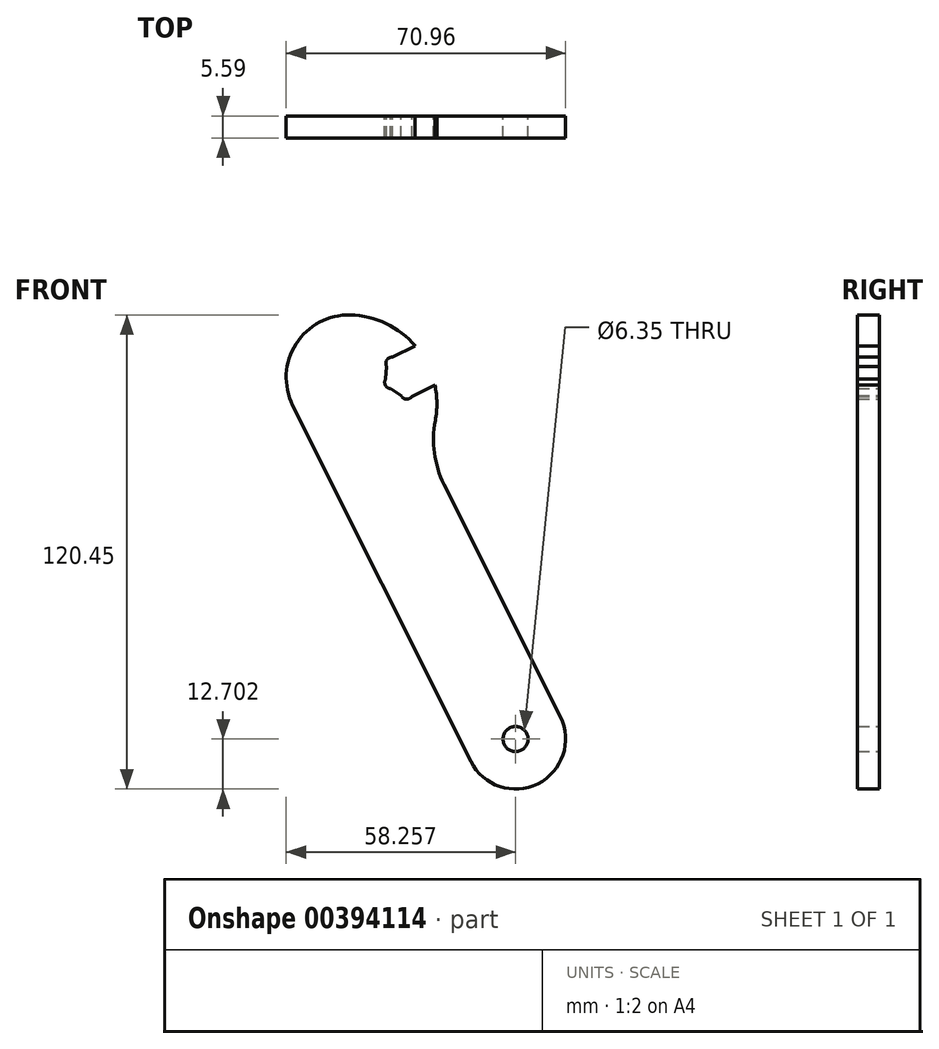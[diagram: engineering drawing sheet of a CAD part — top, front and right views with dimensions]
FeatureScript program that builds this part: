
annotation { "Feature Type Name" : "Feature", "Feature Type Description" : "" }
export const myFeature = defineFeature(function(context is Context, id is Id, definition is map)
    precondition{}
    {
        {
            var Q0;
            Q0=qCreatedBy(makeId("Front.planeOp"),FACE);
            var sketch = newSketch(context, id + "F0", { "sketchPlane" : qUnion([Q0])});
            skCircle(sketch, "E0", {"center": v(-169.2, -191.67) * mm, "radius": 3.18 * mm, "construction": true});
            skCircle(sketch, "E1.0.1.0", {"center": v(-169.2, -166.27) * mm, "radius": 3.18 * mm, "construction": true});
            skCircle(sketch, "E1.0.2.0", {"center": v(-169.2, -140.87) * mm, "radius": 3.18 * mm, "construction": true});
            skCircle(sketch, "E1.0.3.0", {"center": v(-169.2, -115.47) * mm, "radius": 3.18 * mm, "construction": true});
            skCircle(sketch, "E1.0.4.0", {"center": v(-169.2, -90.07) * mm, "radius": 3.18 * mm, "construction": true});
            skCircle(sketch, "E1.0.5.0", {"center": v(-169.2, -64.67) * mm, "radius": 3.18 * mm, "construction": true});
            skCircle(sketch, "E1.0.6.0", {"center": v(-169.2, -39.27) * mm, "radius": 3.18 * mm, "construction": true});
            skCircle(sketch, "E1.0.7.0", {"center": v(-169.2, -13.87) * mm, "radius": 3.18 * mm, "construction": true});
            skCircle(sketch, "E1.0.8.0", {"center": v(-169.2, 11.53) * mm, "radius": 3.18 * mm, "construction": true});
            skCircle(sketch, "E1.0.9.0", {"center": v(-169.2, 36.93) * mm, "radius": 3.18 * mm, "construction": true});
            skCircle(sketch, "E1.0.10.0", {"center": v(-169.2, 62.33) * mm, "radius": 3.18 * mm, "construction": true});
            skCircle(sketch, "E1.0.11.0", {"center": v(-169.2, 87.73) * mm, "radius": 3.18 * mm, "construction": true});
            skCircle(sketch, "E1.0.12.0", {"center": v(-169.2, 113.13) * mm, "radius": 3.18 * mm, "construction": true});
            skCircle(sketch, "E1.0.13.0", {"center": v(-169.2, 138.53) * mm, "radius": 3.18 * mm, "construction": true});
            skCircle(sketch, "E1.0.14.0", {"center": v(-169.2, 163.93) * mm, "radius": 3.18 * mm, "construction": true});
            skCircle(sketch, "E1.1.0.0", {"center": v(-143.8, -191.67) * mm, "radius": 3.18 * mm, "construction": true});
            skCircle(sketch, "E1.1.1.0", {"center": v(-143.8, -166.27) * mm, "radius": 3.18 * mm, "construction": true});
            skCircle(sketch, "E1.1.2.0", {"center": v(-143.8, -140.87) * mm, "radius": 3.18 * mm, "construction": true});
            skCircle(sketch, "E1.1.3.0", {"center": v(-143.8, -115.47) * mm, "radius": 3.18 * mm, "construction": true});
            skCircle(sketch, "E1.1.4.0", {"center": v(-143.8, -90.07) * mm, "radius": 3.18 * mm, "construction": true});
            skCircle(sketch, "E1.1.5.0", {"center": v(-143.8, -64.67) * mm, "radius": 3.18 * mm, "construction": true});
            skCircle(sketch, "E1.1.6.0", {"center": v(-143.8, -39.27) * mm, "radius": 3.18 * mm, "construction": true});
            skCircle(sketch, "E1.1.7.0", {"center": v(-143.8, -13.87) * mm, "radius": 3.18 * mm, "construction": true});
            skCircle(sketch, "E1.1.8.0", {"center": v(-143.8, 11.53) * mm, "radius": 3.18 * mm, "construction": true});
            skCircle(sketch, "E1.1.9.0", {"center": v(-143.8, 36.93) * mm, "radius": 3.18 * mm, "construction": true});
            skCircle(sketch, "E1.1.10.0", {"center": v(-143.8, 62.33) * mm, "radius": 3.18 * mm, "construction": true});
            skCircle(sketch, "E1.1.11.0", {"center": v(-143.8, 87.73) * mm, "radius": 3.18 * mm, "construction": true});
            skCircle(sketch, "E1.1.12.0", {"center": v(-143.8, 113.13) * mm, "radius": 3.18 * mm, "construction": true});
            skCircle(sketch, "E1.1.13.0", {"center": v(-143.8, 138.53) * mm, "radius": 3.18 * mm, "construction": true});
            skCircle(sketch, "E1.1.14.0", {"center": v(-143.8, 163.93) * mm, "radius": 3.18 * mm, "construction": true});
            skCircle(sketch, "E1.2.0.0", {"center": v(-118.4, -191.67) * mm, "radius": 3.18 * mm, "construction": true});
            skCircle(sketch, "E1.2.1.0", {"center": v(-118.4, -166.27) * mm, "radius": 3.18 * mm, "construction": true});
            skCircle(sketch, "E1.2.2.0", {"center": v(-118.4, -140.87) * mm, "radius": 3.18 * mm, "construction": true});
            skCircle(sketch, "E1.2.3.0", {"center": v(-118.4, -115.47) * mm, "radius": 3.18 * mm, "construction": true});
            skCircle(sketch, "E1.2.4.0", {"center": v(-118.4, -90.07) * mm, "radius": 3.18 * mm, "construction": true});
            skCircle(sketch, "E1.2.5.0", {"center": v(-118.4, -64.67) * mm, "radius": 3.18 * mm, "construction": true});
            skCircle(sketch, "E1.2.6.0", {"center": v(-118.4, -39.27) * mm, "radius": 3.18 * mm, "construction": true});
            skCircle(sketch, "E1.2.7.0", {"center": v(-118.4, -13.87) * mm, "radius": 3.18 * mm, "construction": true});
            skCircle(sketch, "E1.2.8.0", {"center": v(-118.4, 11.53) * mm, "radius": 3.18 * mm, "construction": true});
            skCircle(sketch, "E1.2.9.0", {"center": v(-118.4, 36.93) * mm, "radius": 3.18 * mm, "construction": true});
            skCircle(sketch, "E1.2.10.0", {"center": v(-118.4, 62.33) * mm, "radius": 3.18 * mm, "construction": true});
            skCircle(sketch, "E1.2.11.0", {"center": v(-118.4, 87.73) * mm, "radius": 3.18 * mm, "construction": true});
            skCircle(sketch, "E1.2.12.0", {"center": v(-118.4, 113.13) * mm, "radius": 3.18 * mm, "construction": true});
            skCircle(sketch, "E1.2.13.0", {"center": v(-118.4, 138.53) * mm, "radius": 3.18 * mm, "construction": true});
            skCircle(sketch, "E1.2.14.0", {"center": v(-118.4, 163.93) * mm, "radius": 3.18 * mm, "construction": true});
            skCircle(sketch, "E1.3.0.0", {"center": v(-93, -191.67) * mm, "radius": 3.18 * mm, "construction": true});
            skCircle(sketch, "E1.3.1.0", {"center": v(-93, -166.27) * mm, "radius": 3.18 * mm, "construction": true});
            skCircle(sketch, "E1.3.2.0", {"center": v(-93, -140.87) * mm, "radius": 3.18 * mm, "construction": true});
            skCircle(sketch, "E1.3.3.0", {"center": v(-93, -115.47) * mm, "radius": 3.18 * mm, "construction": true});
            skCircle(sketch, "E1.3.4.0", {"center": v(-93, -90.07) * mm, "radius": 3.18 * mm, "construction": true});
            skCircle(sketch, "E1.3.5.0", {"center": v(-93, -64.67) * mm, "radius": 3.18 * mm, "construction": true});
            skCircle(sketch, "E1.3.6.0", {"center": v(-93, -39.27) * mm, "radius": 3.18 * mm, "construction": true});
            skCircle(sketch, "E1.3.7.0", {"center": v(-93, -13.87) * mm, "radius": 3.18 * mm, "construction": true});
            skCircle(sketch, "E1.3.8.0", {"center": v(-93, 11.53) * mm, "radius": 3.18 * mm, "construction": true});
            skCircle(sketch, "E1.3.9.0", {"center": v(-93, 36.93) * mm, "radius": 3.18 * mm, "construction": true});
            skCircle(sketch, "E1.3.10.0", {"center": v(-93, 62.33) * mm, "radius": 3.18 * mm, "construction": true});
            skCircle(sketch, "E1.3.11.0", {"center": v(-93, 87.73) * mm, "radius": 3.18 * mm, "construction": true});
            skCircle(sketch, "E1.3.12.0", {"center": v(-93, 113.13) * mm, "radius": 3.18 * mm, "construction": true});
            skCircle(sketch, "E1.3.13.0", {"center": v(-93, 138.53) * mm, "radius": 3.18 * mm, "construction": true});
            skCircle(sketch, "E1.3.14.0", {"center": v(-93, 163.93) * mm, "radius": 3.18 * mm, "construction": true});
            skCircle(sketch, "E1.4.0.0", {"center": v(-67.6, -191.67) * mm, "radius": 3.18 * mm, "construction": true});
            skCircle(sketch, "E1.4.1.0", {"center": v(-67.6, -166.27) * mm, "radius": 3.18 * mm, "construction": true});
            skCircle(sketch, "E1.4.2.0", {"center": v(-67.6, -140.87) * mm, "radius": 3.18 * mm, "construction": true});
            skCircle(sketch, "E1.4.3.0", {"center": v(-67.6, -115.47) * mm, "radius": 3.18 * mm, "construction": true});
            skCircle(sketch, "E1.4.4.0", {"center": v(-67.6, -90.07) * mm, "radius": 3.18 * mm, "construction": true});
            skCircle(sketch, "E1.4.5.0", {"center": v(-67.6, -64.67) * mm, "radius": 3.18 * mm, "construction": true});
            skCircle(sketch, "E1.4.6.0", {"center": v(-67.6, -39.27) * mm, "radius": 3.18 * mm, "construction": true});
            skCircle(sketch, "E1.4.7.0", {"center": v(-67.6, -13.87) * mm, "radius": 3.18 * mm, "construction": true});
            skCircle(sketch, "E1.4.8.0", {"center": v(-67.6, 11.53) * mm, "radius": 3.18 * mm, "construction": true});
            skCircle(sketch, "E1.4.9.0", {"center": v(-67.6, 36.93) * mm, "radius": 3.18 * mm, "construction": true});
            skCircle(sketch, "E1.4.10.0", {"center": v(-67.6, 62.33) * mm, "radius": 3.18 * mm, "construction": true});
            skCircle(sketch, "E1.4.11.0", {"center": v(-67.6, 87.73) * mm, "radius": 3.18 * mm, "construction": true});
            skCircle(sketch, "E1.4.12.0", {"center": v(-67.6, 113.13) * mm, "radius": 3.18 * mm, "construction": true});
            skCircle(sketch, "E1.4.13.0", {"center": v(-67.6, 138.53) * mm, "radius": 3.18 * mm, "construction": true});
            skCircle(sketch, "E1.4.14.0", {"center": v(-67.6, 163.93) * mm, "radius": 3.18 * mm, "construction": true});
            skCircle(sketch, "E1.5.0.0", {"center": v(-42.2, -191.67) * mm, "radius": 3.18 * mm, "construction": true});
            skCircle(sketch, "E1.5.1.0", {"center": v(-42.2, -166.27) * mm, "radius": 3.18 * mm, "construction": true});
            skCircle(sketch, "E1.5.2.0", {"center": v(-42.2, -140.87) * mm, "radius": 3.18 * mm, "construction": true});
            skCircle(sketch, "E1.5.3.0", {"center": v(-42.2, -115.47) * mm, "radius": 3.18 * mm, "construction": true});
            skCircle(sketch, "E1.5.4.0", {"center": v(-42.2, -90.07) * mm, "radius": 3.18 * mm, "construction": true});
            skCircle(sketch, "E1.5.5.0", {"center": v(-42.2, -64.67) * mm, "radius": 3.18 * mm, "construction": true});
            skCircle(sketch, "E1.5.6.0", {"center": v(-42.2, -39.27) * mm, "radius": 3.18 * mm, "construction": true});
            skCircle(sketch, "E1.5.7.0", {"center": v(-42.2, -13.87) * mm, "radius": 3.18 * mm, "construction": true});
            skCircle(sketch, "E1.5.8.0", {"center": v(-42.2, 11.53) * mm, "radius": 3.18 * mm, "construction": true});
            skCircle(sketch, "E1.5.9.0", {"center": v(-42.2, 36.93) * mm, "radius": 3.18 * mm, "construction": true});
            skCircle(sketch, "E1.5.10.0", {"center": v(-42.2, 62.33) * mm, "radius": 3.18 * mm, "construction": true});
            skCircle(sketch, "E1.5.11.0", {"center": v(-42.2, 87.73) * mm, "radius": 3.18 * mm, "construction": true});
            skCircle(sketch, "E1.5.12.0", {"center": v(-42.2, 113.13) * mm, "radius": 3.18 * mm, "construction": true});
            skCircle(sketch, "E1.5.13.0", {"center": v(-42.2, 138.53) * mm, "radius": 3.18 * mm, "construction": true});
            skCircle(sketch, "E1.5.14.0", {"center": v(-42.2, 163.93) * mm, "radius": 3.18 * mm, "construction": true});
            skCircle(sketch, "E1.6.0.0", {"center": v(-16.8, -191.67) * mm, "radius": 3.18 * mm, "construction": true});
            skCircle(sketch, "E1.6.1.0", {"center": v(-16.8, -166.27) * mm, "radius": 3.18 * mm, "construction": true});
            skCircle(sketch, "E1.6.2.0", {"center": v(-16.8, -140.87) * mm, "radius": 3.18 * mm, "construction": true});
            skCircle(sketch, "E1.6.3.0", {"center": v(-16.8, -115.47) * mm, "radius": 3.18 * mm, "construction": true});
            skCircle(sketch, "E1.6.4.0", {"center": v(-16.8, -90.07) * mm, "radius": 3.18 * mm, "construction": true});
            skCircle(sketch, "E1.6.5.0", {"center": v(-16.8, -64.67) * mm, "radius": 3.18 * mm, "construction": true});
            skCircle(sketch, "E1.6.6.0", {"center": v(-16.8, -39.27) * mm, "radius": 3.18 * mm, "construction": true});
            skCircle(sketch, "E1.6.7.0", {"center": v(-16.8, -13.87) * mm, "radius": 3.18 * mm, "construction": true});
            skCircle(sketch, "E1.6.8.0", {"center": v(-16.8, 11.53) * mm, "radius": 3.18 * mm, "construction": true});
            skCircle(sketch, "E1.6.9.0", {"center": v(-16.8, 36.93) * mm, "radius": 3.18 * mm, "construction": true});
            skCircle(sketch, "E1.6.10.0", {"center": v(-16.8, 62.33) * mm, "radius": 3.18 * mm, "construction": true});
            skCircle(sketch, "E1.6.11.0", {"center": v(-16.8, 87.73) * mm, "radius": 3.18 * mm, "construction": true});
            skCircle(sketch, "E1.6.12.0", {"center": v(-16.8, 113.13) * mm, "radius": 3.18 * mm, "construction": true});
            skCircle(sketch, "E1.6.13.0", {"center": v(-16.8, 138.53) * mm, "radius": 3.18 * mm, "construction": true});
            skCircle(sketch, "E1.6.14.0", {"center": v(-16.8, 163.93) * mm, "radius": 3.18 * mm, "construction": true});
            skCircle(sketch, "E1.7.0.0", {"center": v(8.6, -191.67) * mm, "radius": 3.18 * mm, "construction": true});
            skCircle(sketch, "E1.7.1.0", {"center": v(8.6, -166.27) * mm, "radius": 3.18 * mm, "construction": true});
            skCircle(sketch, "E1.7.2.0", {"center": v(8.6, -140.87) * mm, "radius": 3.18 * mm, "construction": true});
            skCircle(sketch, "E1.7.3.0", {"center": v(8.6, -115.47) * mm, "radius": 3.18 * mm, "construction": true});
            skCircle(sketch, "E1.7.4.0", {"center": v(8.6, -90.07) * mm, "radius": 3.18 * mm, "construction": true});
            skCircle(sketch, "E1.7.5.0", {"center": v(8.6, -64.67) * mm, "radius": 3.18 * mm, "construction": true});
            skCircle(sketch, "E1.7.6.0", {"center": v(8.6, -39.27) * mm, "radius": 3.18 * mm, "construction": true});
            skCircle(sketch, "E1.7.7.0", {"center": v(8.6, -13.87) * mm, "radius": 3.18 * mm, "construction": true});
            skCircle(sketch, "E1.7.8.0", {"center": v(8.6, 11.53) * mm, "radius": 3.18 * mm, "construction": true});
            skCircle(sketch, "E1.7.9.0", {"center": v(8.6, 36.93) * mm, "radius": 3.18 * mm, "construction": true});
            skCircle(sketch, "E1.7.10.0", {"center": v(8.6, 62.33) * mm, "radius": 3.18 * mm, "construction": true});
            skCircle(sketch, "E1.7.11.0", {"center": v(8.6, 87.73) * mm, "radius": 3.18 * mm, "construction": true});
            skCircle(sketch, "E1.7.12.0", {"center": v(8.6, 113.13) * mm, "radius": 3.18 * mm, "construction": true});
            skCircle(sketch, "E1.7.13.0", {"center": v(8.6, 138.53) * mm, "radius": 3.18 * mm, "construction": true});
            skCircle(sketch, "E1.7.14.0", {"center": v(8.6, 163.93) * mm, "radius": 3.18 * mm, "construction": true});
            skCircle(sketch, "E1.8.0.0", {"center": v(34, -191.67) * mm, "radius": 3.18 * mm, "construction": true});
            skCircle(sketch, "E1.8.1.0", {"center": v(34, -166.27) * mm, "radius": 3.18 * mm, "construction": true});
            skCircle(sketch, "E1.8.2.0", {"center": v(34, -140.87) * mm, "radius": 3.18 * mm, "construction": true});
            skCircle(sketch, "E1.8.3.0", {"center": v(34, -115.47) * mm, "radius": 3.18 * mm, "construction": true});
            skCircle(sketch, "E1.8.4.0", {"center": v(34, -90.07) * mm, "radius": 3.18 * mm, "construction": true});
            skCircle(sketch, "E1.8.5.0", {"center": v(34, -64.67) * mm, "radius": 3.18 * mm, "construction": true});
            skCircle(sketch, "E1.8.6.0", {"center": v(34, -39.27) * mm, "radius": 3.18 * mm, "construction": true});
            skCircle(sketch, "E1.8.7.0", {"center": v(34, -13.87) * mm, "radius": 3.18 * mm, "construction": true});
            skCircle(sketch, "E1.8.8.0", {"center": v(34, 11.53) * mm, "radius": 3.18 * mm, "construction": true});
            skCircle(sketch, "E1.8.9.0", {"center": v(34, 36.93) * mm, "radius": 3.18 * mm, "construction": true});
            skCircle(sketch, "E1.8.10.0", {"center": v(34, 62.33) * mm, "radius": 3.18 * mm, "construction": true});
            skCircle(sketch, "E1.8.11.0", {"center": v(34, 87.73) * mm, "radius": 3.18 * mm, "construction": true});
            skCircle(sketch, "E1.8.12.0", {"center": v(34, 113.13) * mm, "radius": 3.18 * mm, "construction": true});
            skCircle(sketch, "E1.8.13.0", {"center": v(34, 138.53) * mm, "radius": 3.18 * mm, "construction": true});
            skCircle(sketch, "E1.8.14.0", {"center": v(34, 163.93) * mm, "radius": 3.18 * mm, "construction": true});
            skCircle(sketch, "E1.9.0.0", {"center": v(59.4, -191.67) * mm, "radius": 3.18 * mm, "construction": true});
            skCircle(sketch, "E1.9.1.0", {"center": v(59.4, -166.27) * mm, "radius": 3.18 * mm, "construction": true});
            skCircle(sketch, "E1.9.2.0", {"center": v(59.4, -140.87) * mm, "radius": 3.18 * mm, "construction": true});
            skCircle(sketch, "E1.9.3.0", {"center": v(59.4, -115.47) * mm, "radius": 3.18 * mm, "construction": true});
            skCircle(sketch, "E1.9.4.0", {"center": v(59.4, -90.07) * mm, "radius": 3.18 * mm, "construction": true});
            skCircle(sketch, "E1.9.5.0", {"center": v(59.4, -64.67) * mm, "radius": 3.18 * mm, "construction": true});
            skCircle(sketch, "E1.9.6.0", {"center": v(59.4, -39.27) * mm, "radius": 3.18 * mm, "construction": true});
            skCircle(sketch, "E1.9.7.0", {"center": v(59.4, -13.87) * mm, "radius": 3.18 * mm, "construction": true});
            skCircle(sketch, "E1.9.8.0", {"center": v(59.4, 11.53) * mm, "radius": 3.18 * mm, "construction": true});
            skCircle(sketch, "E1.9.9.0", {"center": v(59.4, 36.93) * mm, "radius": 3.18 * mm, "construction": true});
            skCircle(sketch, "E1.9.10.0", {"center": v(59.4, 62.33) * mm, "radius": 3.18 * mm, "construction": true});
            skCircle(sketch, "E1.9.11.0", {"center": v(59.4, 87.73) * mm, "radius": 3.18 * mm, "construction": true});
            skCircle(sketch, "E1.9.12.0", {"center": v(59.4, 113.13) * mm, "radius": 3.18 * mm, "construction": true});
            skCircle(sketch, "E1.9.13.0", {"center": v(59.4, 138.53) * mm, "radius": 3.18 * mm, "construction": true});
            skCircle(sketch, "E1.9.14.0", {"center": v(59.4, 163.93) * mm, "radius": 3.18 * mm, "construction": true});
            skCircle(sketch, "E1.10.0.0", {"center": v(84.8, -191.67) * mm, "radius": 3.18 * mm, "construction": true});
            skCircle(sketch, "E1.10.1.0", {"center": v(84.8, -166.27) * mm, "radius": 3.18 * mm, "construction": true});
            skCircle(sketch, "E1.10.2.0", {"center": v(84.8, -140.87) * mm, "radius": 3.18 * mm, "construction": true});
            skCircle(sketch, "E1.10.3.0", {"center": v(84.8, -115.47) * mm, "radius": 3.18 * mm, "construction": true});
            skCircle(sketch, "E1.10.4.0", {"center": v(84.8, -90.07) * mm, "radius": 3.18 * mm, "construction": true});
            skCircle(sketch, "E1.10.5.0", {"center": v(84.8, -64.67) * mm, "radius": 3.18 * mm, "construction": true});
            skCircle(sketch, "E1.10.6.0", {"center": v(84.8, -39.27) * mm, "radius": 3.18 * mm, "construction": true});
            skCircle(sketch, "E1.10.7.0", {"center": v(84.8, -13.87) * mm, "radius": 3.18 * mm, "construction": true});
            skCircle(sketch, "E1.10.8.0", {"center": v(84.8, 11.53) * mm, "radius": 3.18 * mm, "construction": true});
            skCircle(sketch, "E1.10.9.0", {"center": v(84.8, 36.93) * mm, "radius": 3.18 * mm, "construction": true});
            skCircle(sketch, "E1.10.10.0", {"center": v(84.8, 62.33) * mm, "radius": 3.18 * mm, "construction": true});
            skCircle(sketch, "E1.10.11.0", {"center": v(84.8, 87.73) * mm, "radius": 3.18 * mm, "construction": true});
            skCircle(sketch, "E1.10.12.0", {"center": v(84.8, 113.13) * mm, "radius": 3.18 * mm, "construction": true});
            skCircle(sketch, "E1.10.13.0", {"center": v(84.8, 138.53) * mm, "radius": 3.18 * mm, "construction": true});
            skCircle(sketch, "E1.10.14.0", {"center": v(84.8, 163.93) * mm, "radius": 3.18 * mm, "construction": true});
            skCircle(sketch, "E1.11.0.0", {"center": v(110.2, -191.67) * mm, "radius": 3.18 * mm, "construction": true});
            skCircle(sketch, "E1.11.1.0", {"center": v(110.2, -166.27) * mm, "radius": 3.18 * mm, "construction": true});
            skCircle(sketch, "E1.11.2.0", {"center": v(110.2, -140.87) * mm, "radius": 3.18 * mm, "construction": true});
            skCircle(sketch, "E1.11.3.0", {"center": v(110.2, -115.47) * mm, "radius": 3.18 * mm, "construction": true});
            skCircle(sketch, "E1.11.4.0", {"center": v(110.2, -90.07) * mm, "radius": 3.18 * mm, "construction": true});
            skCircle(sketch, "E1.11.5.0", {"center": v(110.2, -64.67) * mm, "radius": 3.18 * mm, "construction": true});
            skCircle(sketch, "E1.11.6.0", {"center": v(110.2, -39.27) * mm, "radius": 3.18 * mm, "construction": true});
            skCircle(sketch, "E1.11.7.0", {"center": v(110.2, -13.87) * mm, "radius": 3.18 * mm, "construction": true});
            skCircle(sketch, "E1.11.8.0", {"center": v(110.2, 11.53) * mm, "radius": 3.18 * mm, "construction": true});
            skCircle(sketch, "E1.11.9.0", {"center": v(110.2, 36.93) * mm, "radius": 3.18 * mm, "construction": true});
            skCircle(sketch, "E1.11.10.0", {"center": v(110.2, 62.33) * mm, "radius": 3.18 * mm, "construction": true});
            skCircle(sketch, "E1.11.11.0", {"center": v(110.2, 87.73) * mm, "radius": 3.18 * mm, "construction": true});
            skCircle(sketch, "E1.11.12.0", {"center": v(110.2, 113.13) * mm, "radius": 3.18 * mm, "construction": true});
            skCircle(sketch, "E1.11.13.0", {"center": v(110.2, 138.53) * mm, "radius": 3.18 * mm, "construction": true});
            skCircle(sketch, "E1.11.14.0", {"center": v(110.2, 163.93) * mm, "radius": 3.18 * mm, "construction": true});
            skCircle(sketch, "E1.12.0.0", {"center": v(135.6, -191.67) * mm, "radius": 3.18 * mm, "construction": true});
            skCircle(sketch, "E1.12.1.0", {"center": v(135.6, -166.27) * mm, "radius": 3.18 * mm, "construction": true});
            skCircle(sketch, "E1.12.2.0", {"center": v(135.6, -140.87) * mm, "radius": 3.18 * mm, "construction": true});
            skCircle(sketch, "E1.12.3.0", {"center": v(135.6, -115.47) * mm, "radius": 3.18 * mm, "construction": true});
            skCircle(sketch, "E1.12.4.0", {"center": v(135.6, -90.07) * mm, "radius": 3.18 * mm, "construction": true});
            skCircle(sketch, "E1.12.5.0", {"center": v(135.6, -64.67) * mm, "radius": 3.18 * mm, "construction": true});
            skCircle(sketch, "E1.12.6.0", {"center": v(135.6, -39.27) * mm, "radius": 3.18 * mm, "construction": true});
            skCircle(sketch, "E1.12.7.0", {"center": v(135.6, -13.87) * mm, "radius": 3.18 * mm, "construction": true});
            skCircle(sketch, "E1.12.8.0", {"center": v(135.6, 11.53) * mm, "radius": 3.18 * mm, "construction": true});
            skCircle(sketch, "E1.12.9.0", {"center": v(135.6, 36.93) * mm, "radius": 3.18 * mm, "construction": true});
            skCircle(sketch, "E1.12.10.0", {"center": v(135.6, 62.33) * mm, "radius": 3.18 * mm, "construction": true});
            skCircle(sketch, "E1.12.11.0", {"center": v(135.6, 87.73) * mm, "radius": 3.18 * mm, "construction": true});
            skCircle(sketch, "E1.12.12.0", {"center": v(135.6, 113.13) * mm, "radius": 3.18 * mm, "construction": true});
            skCircle(sketch, "E1.12.13.0", {"center": v(135.6, 138.53) * mm, "radius": 3.18 * mm, "construction": true});
            skCircle(sketch, "E1.12.14.0", {"center": v(135.6, 163.93) * mm, "radius": 3.18 * mm, "construction": true});
            skCircle(sketch, "E1.13.0.0", {"center": v(161, -191.67) * mm, "radius": 3.18 * mm, "construction": true});
            skCircle(sketch, "E1.13.1.0", {"center": v(161, -166.27) * mm, "radius": 3.18 * mm, "construction": true});
            skCircle(sketch, "E1.13.2.0", {"center": v(161, -140.87) * mm, "radius": 3.18 * mm, "construction": true});
            skCircle(sketch, "E1.13.3.0", {"center": v(161, -115.47) * mm, "radius": 3.18 * mm, "construction": true});
            skCircle(sketch, "E1.13.4.0", {"center": v(161, -90.07) * mm, "radius": 3.18 * mm, "construction": true});
            skCircle(sketch, "E1.13.5.0", {"center": v(161, -64.67) * mm, "radius": 3.18 * mm, "construction": true});
            skCircle(sketch, "E1.13.6.0", {"center": v(161, -39.27) * mm, "radius": 3.18 * mm, "construction": true});
            skCircle(sketch, "E1.13.7.0", {"center": v(161, -13.87) * mm, "radius": 3.18 * mm, "construction": true});
            skCircle(sketch, "E1.13.8.0", {"center": v(161, 11.53) * mm, "radius": 3.18 * mm, "construction": true});
            skCircle(sketch, "E1.13.9.0", {"center": v(161, 36.93) * mm, "radius": 3.18 * mm, "construction": true});
            skCircle(sketch, "E1.13.10.0", {"center": v(161, 62.33) * mm, "radius": 3.18 * mm, "construction": true});
            skCircle(sketch, "E1.13.11.0", {"center": v(161, 87.73) * mm, "radius": 3.18 * mm, "construction": true});
            skCircle(sketch, "E1.13.12.0", {"center": v(161, 113.13) * mm, "radius": 3.18 * mm, "construction": true});
            skCircle(sketch, "E1.13.13.0", {"center": v(161, 138.53) * mm, "radius": 3.18 * mm, "construction": true});
            skCircle(sketch, "E1.13.14.0", {"center": v(161, 163.93) * mm, "radius": 3.18 * mm, "construction": true});
            skCircle(sketch, "E1.14.0.0", {"center": v(186.4, -191.67) * mm, "radius": 3.18 * mm, "construction": true});
            skCircle(sketch, "E1.14.1.0", {"center": v(186.4, -166.27) * mm, "radius": 3.18 * mm, "construction": true});
            skCircle(sketch, "E1.14.2.0", {"center": v(186.4, -140.87) * mm, "radius": 3.18 * mm, "construction": true});
            skCircle(sketch, "E1.14.3.0", {"center": v(186.4, -115.47) * mm, "radius": 3.18 * mm, "construction": true});
            skCircle(sketch, "E1.14.4.0", {"center": v(186.4, -90.07) * mm, "radius": 3.18 * mm, "construction": true});
            skCircle(sketch, "E1.14.5.0", {"center": v(186.4, -64.67) * mm, "radius": 3.18 * mm, "construction": true});
            skCircle(sketch, "E1.14.6.0", {"center": v(186.4, -39.27) * mm, "radius": 3.18 * mm, "construction": true});
            skCircle(sketch, "E1.14.7.0", {"center": v(186.4, -13.87) * mm, "radius": 3.18 * mm, "construction": true});
            skCircle(sketch, "E1.14.8.0", {"center": v(186.4, 11.53) * mm, "radius": 3.18 * mm, "construction": true});
            skCircle(sketch, "E1.14.9.0", {"center": v(186.4, 36.93) * mm, "radius": 3.18 * mm, "construction": true});
            skCircle(sketch, "E1.14.10.0", {"center": v(186.4, 62.33) * mm, "radius": 3.18 * mm, "construction": true});
            skCircle(sketch, "E1.14.11.0", {"center": v(186.4, 87.73) * mm, "radius": 3.18 * mm, "construction": true});
            skCircle(sketch, "E1.14.12.0", {"center": v(186.4, 113.13) * mm, "radius": 3.18 * mm, "construction": true});
            skCircle(sketch, "E1.14.13.0", {"center": v(186.4, 138.53) * mm, "radius": 3.18 * mm, "construction": true});
            skCircle(sketch, "E1.14.14.0", {"center": v(186.4, 163.93) * mm, "radius": 3.18 * mm, "construction": true});
            skLineSegment(sketch, "E1.direction1", {"start": v(-169.2, -191.67) * mm, "end": v(-143.8, -191.67) * mm, "construction": true});
            skLineSegment(sketch, "E1.direction2", {"start": v(-169.2, -191.67) * mm, "end": v(-169.2, -166.27) * mm, "construction": true});
            skLineSegment(sketch, "E2", {"start": v(-118.4, -191.67) * mm, "end": v(-143.8, -191.67) * mm, "construction": true});
            skLineSegment(sketch, "E3", {"start": v(-93, -191.67) * mm, "end": v(-118.4, -166.27) * mm, "construction": true});
            skLineSegment(sketch, "E4", {"start": v(-93, -166.27) * mm, "end": v(-118.4, -166.27) * mm, "construction": true});
            skLineSegment(sketch, "E5", {"start": v(-105.7, -166.27) * mm, "end": v(-105.7, -172.04) * mm});
            skLineSegment(sketch, "E6", {"start": v(-112.6, -178.37) * mm, "end": v(-131.1, -176.75) * mm});
            skLineSegment(sketch, "E7", {"start": v(-131.1, -176.75) * mm, "end": v(-131.1, -191.67) * mm});
            skPoint(sketch, "E8.visualSharp", {"position": v(-105.7, -178.97) * mm});
            skArc(sketch, "E8.filletArc", {"start": v(-112.6, -178.37) * mm, "mid": v(-107.75, -176.72) * mm, "end": v(-105.7, -172.04) * mm});
            skLineSegment(sketch, "E9.0.1.0", {"start": v(-131.1, -151.35) * mm, "end": v(-131.1, -166.27) * mm, "construction": true});
            skLineSegment(sketch, "E9.1.0.0", {"start": v(-105.7, -176.75) * mm, "end": v(-105.7, -191.67) * mm, "construction": true});
            skLineSegment(sketch, "E9.1.1.0", {"start": v(-105.7, -151.35) * mm, "end": v(-105.7, -166.27) * mm});
            skLineSegment(sketch, "E9.1.1.1", {"start": v(-87.2, -152.97) * mm, "end": v(-105.7, -151.35) * mm});
            skArc(sketch, "E9.1.1.2", {"start": v(-87.2, -152.97) * mm, "mid": v(-82.35, -151.32) * mm, "end": v(-80.3, -146.64) * mm});
            skLineSegment(sketch, "E9.1.1.3", {"start": v(-80.3, -140.87) * mm, "end": v(-80.3, -146.64) * mm});
            skLineSegment(sketch, "E9.2.2.0", {"start": v(-80.3, -125.95) * mm, "end": v(-80.3, -140.87) * mm});
            skLineSegment(sketch, "E9.2.2.1", {"start": v(-61.8, -127.57) * mm, "end": v(-80.3, -125.95) * mm});
            skArc(sketch, "E9.2.2.2", {"start": v(-61.8, -127.57) * mm, "mid": v(-56.95, -125.92) * mm, "end": v(-54.9, -121.24) * mm});
            skLineSegment(sketch, "E9.2.2.3", {"start": v(-54.9, -115.47) * mm, "end": v(-54.9, -121.24) * mm});
            skLineSegment(sketch, "E9.3.3.0", {"start": v(-54.9, -100.55) * mm, "end": v(-54.9, -115.47) * mm});
            skLineSegment(sketch, "E9.3.3.1", {"start": v(-36.4, -102.17) * mm, "end": v(-54.9, -100.55) * mm});
            skArc(sketch, "E9.3.3.2", {"start": v(-36.4, -102.17) * mm, "mid": v(-31.55, -100.52) * mm, "end": v(-29.5, -95.84) * mm});
            skLineSegment(sketch, "E9.3.3.3", {"start": v(-29.5, -90.07) * mm, "end": v(-29.5, -95.84) * mm});
            skLineSegment(sketch, "E9.4.4.0", {"start": v(-29.5, -75.15) * mm, "end": v(-29.5, -90.07) * mm});
            skLineSegment(sketch, "E9.4.4.1", {"start": v(-4.1, -77.37) * mm, "end": v(-29.5, -75.15) * mm});
            skLineSegment(sketch, "E9.direction1", {"start": v(-131.1, -191.67) * mm, "end": v(-105.7, -191.67) * mm, "construction": true});
            skLineSegment(sketch, "E9.direction2", {"start": v(-131.1, -191.67) * mm, "end": v(-131.1, -166.27) * mm, "construction": true});
            skCircle(sketch, "E10", {"center": v(-42.2, -140.87) * mm, "radius": 19.05 * mm});
            skLineSegment(sketch, "E11", {"start": v(-131.1, -191.67) * mm, "end": v(-64.42, -191.67) * mm});
            skLineSegment(sketch, "E12", {"start": v(-64.42, -191.67) * mm, "end": v(-4.1, -132.4) * mm});
            skLineSegment(sketch, "E13", {"start": v(-4.1, -132.4) * mm, "end": v(-4.1, -77.37) * mm});
            skPoint(sketch, "E14.orphan", {"position": v(-11, -76.77) * mm});
            skCircle(sketch, "E15", {"center": v(-67.6, -166.27) * mm, "radius": 3.18 * mm});
            skCircle(sketch, "E16", {"center": v(-16.8, -115.47) * mm, "radius": 3.18 * mm});
            skSolve(sketch);
        }
        {
            var Q0;
            Q0=qCreatedBy(makeId("Front.planeOp"),FACE);
            var sketch = newSketch(context, id + "F1", { "sketchPlane" : qUnion([Q0])});
            skLineSegment(sketch, "E17", {"start": v(-169.2, 163.93) * mm, "end": v(-184.43, 156.3) * mm, "construction": true});
            skLineSegment(sketch, "E18", {"start": v(-184.43, 156.3) * mm, "end": v(-169.2, 62.33) * mm, "construction": true});
            skLineSegment(sketch, "E19", {"start": v(-184.43, 156.3) * mm, "end": v(-118.4, 87.73) * mm, "construction": true});
            skLineSegment(sketch, "E20", {"start": v(-184.43, 156.3) * mm, "end": v(-141.85, 71.15) * mm, "construction": true});
            skCircle(sketch, "E21.cCircle", {"center": v(-169.2, 163.93) * mm, "radius": 5.56 * mm, "construction": true});
            skLineSegment(sketch, "E21.0", {"start": v(-170.92, 158.41) * mm, "end": v(-173.58, 160.17) * mm});
            skLineSegment(sketch, "E21.1", {"start": v(-174.83, 162.67) * mm, "end": v(-174.64, 165.85) * mm});
            skLineSegment(sketch, "E21.2", {"start": v(-173.1, 168.18) * mm, "end": v(-167.33, 171.07) * mm});
            skLineSegment(sketch, "E21.5", {"start": v(-162.36, 161.13) * mm, "end": v(-168.13, 158.24) * mm});
            skPoint(sketch, "E21.0.midPoint", {"position": v(-172.25, 159.3) * mm});
            skArc(sketch, "E22", {"start": v(-162.24, 152.04) * mm, "mid": v(-161.84, 156.6) * mm, "end": v(-162.36, 161.13) * mm});
            skArc(sketch, "E23", {"start": v(-173.1, 168.18) * mm, "mid": v(-174.54, 167.46) * mm, "end": v(-174.64, 165.85) * mm});
            skLineSegment(sketch, "E24", {"start": v(-174.54, 167.46) * mm, "end": v(-173.2, 166.57) * mm, "construction": true});
            skArc(sketch, "E25.1.0", {"start": v(-174.83, 162.67) * mm, "mid": v(-174.93, 161.06) * mm, "end": v(-173.58, 160.17) * mm});
            skArc(sketch, "E25.2.0", {"start": v(-170.92, 158.41) * mm, "mid": v(-169.58, 157.52) * mm, "end": v(-168.13, 158.24) * mm});
            skLineSegment(sketch, "E25.anchor1", {"start": v(-169.2, 163.93) * mm, "end": v(-174.64, 165.85) * mm, "construction": true});
            skLineSegment(sketch, "E25.anchor2", {"start": v(-169.2, 163.93) * mm, "end": v(-168.13, 158.24) * mm, "construction": true});
            skCircle(sketch, "E26", {"center": v(-141.85, 71.15) * mm, "radius": 3.18 * mm});
            skArc(sketch, "E27", {"start": v(-153.21, 65.47) * mm, "mid": v(-136.17, 59.8) * mm, "end": v(-130.5, 76.83) * mm});
            skLineSegment(sketch, "E28", {"start": v(-130.5, 76.83) * mm, "end": v(-160.02, 135.88) * mm});
            skPoint(sketch, "E28.endSnap0", {"position": v(-163.14, 113.73) * mm});
            skLineSegment(sketch, "E29", {"start": v(-153.21, 65.47) * mm, "end": v(-198.44, 155.93) * mm});
            skArc(sketch, "E30.trimOffspring", {"start": v(-167.33, 171.07) * mm, "mid": v(-174.73, 176.72) * mm, "end": v(-183.79, 178.9) * mm});
            skPoint(sketch, "E31.visualSharp", {"position": v(-164.71, 145.27) * mm});
            skArc(sketch, "E31.filletArc", {"start": v(-162.24, 152.04) * mm, "mid": v(-162.46, 143.78) * mm, "end": v(-160.02, 135.88) * mm});
            skPoint(sketch, "E32.visualSharp", {"position": v(-204.15, 167.34) * mm});
            skArc(sketch, "E32.filletArc", {"start": v(-183.79, 178.9) * mm, "mid": v(-197.62, 171.56) * mm, "end": v(-198.44, 155.93) * mm});
            skPoint(sketch, "E33.orphan", {"position": v(-174.93, 161.06) * mm});
            skPoint(sketch, "E34.orphan", {"position": v(-169.58, 157.52) * mm});
            skLineSegment(sketch, "E35", {"start": v(-184.43, 156.3) * mm, "end": v(-184.43, 78.18) * mm, "construction": true});
            skSolve(sketch);
        }
        {
            var Q0;
            Q0 = qSketchRegion(id + "F1", true);
            extrude(context, id + "F2", {"entities" : qUnion([Q0]), "depth" : 5.6 * mm});
        }
    });
